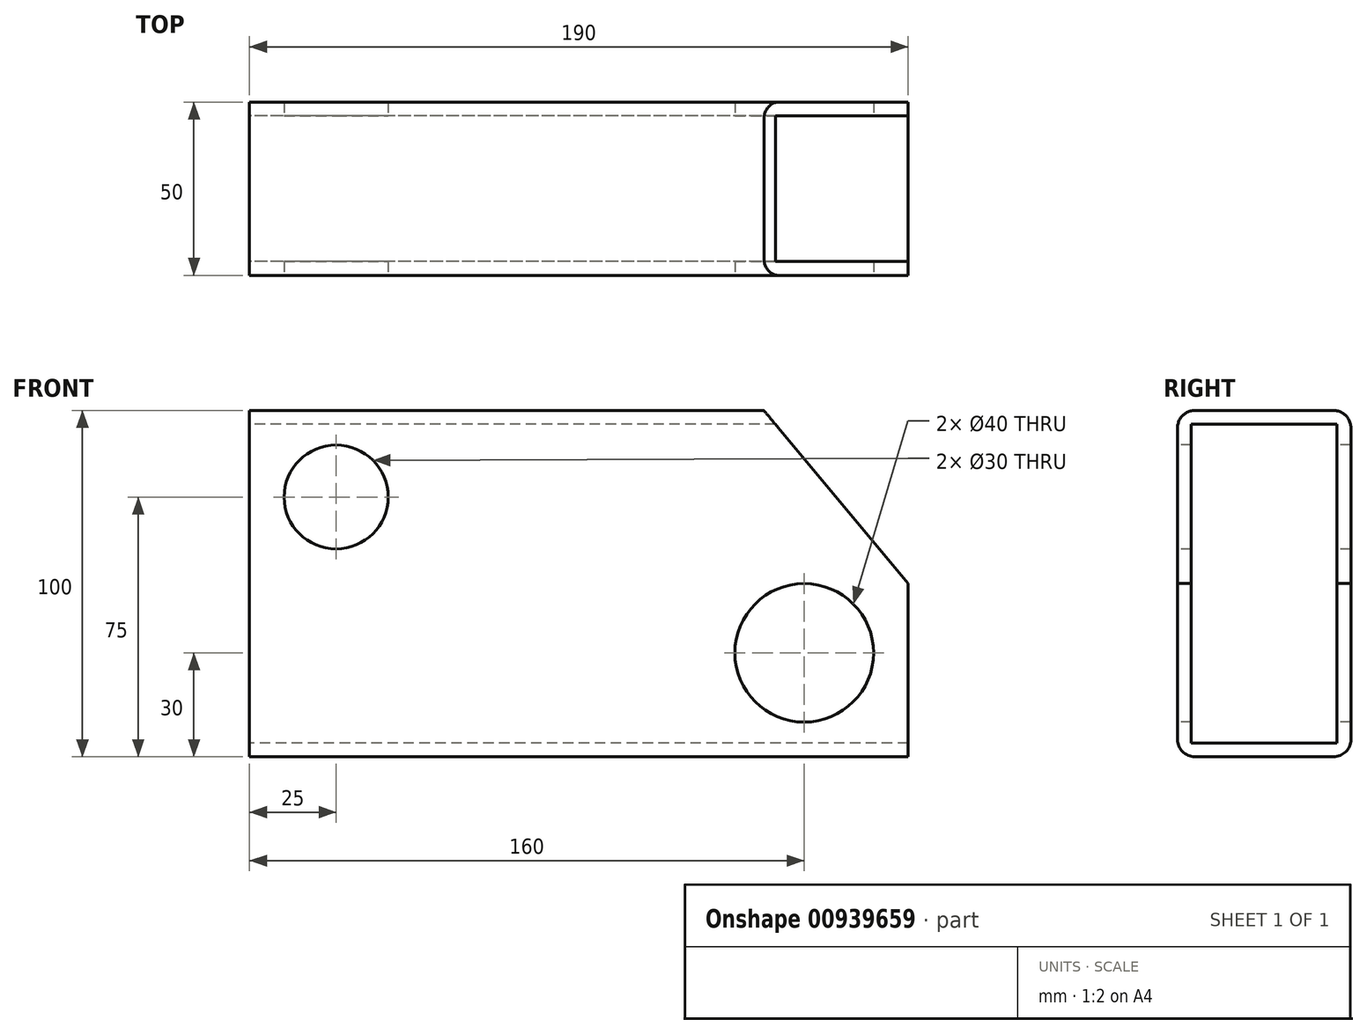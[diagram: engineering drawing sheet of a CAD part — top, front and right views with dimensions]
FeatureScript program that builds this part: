
annotation { "Feature Type Name" : "Feature", "Feature Type Description" : "" }
export const myFeature = defineFeature(function(context is Context, id is Id, definition is map)
    precondition{}
    {
        {
            var Q0;
            Q0=qCreatedBy(makeId("Front.planeOp"),FACE);
            var sketch = newSketch(context, id + "F0", { "sketchPlane" : qUnion([Q0])});
            skLineSegment(sketch, "E0.bottom", {"start": v(95, -50) * mm, "end": v(-95, -50) * mm});
            skLineSegment(sketch, "E0.top", {"start": v(53.36, 50) * mm, "end": v(-95, 50) * mm});
            skLineSegment(sketch, "E0.left", {"start": v(95, -50) * mm, "end": v(95, 0) * mm});
            skLineSegment(sketch, "E0.right", {"start": v(-95, -50) * mm, "end": v(-95, 50) * mm});
            skPoint(sketch, "E0.middle", {"position": v(0, 0) * mm});
            skLineSegment(sketch, "E1", {"start": v(53.36, 50) * mm, "end": v(95, 0) * mm});
            skPoint(sketch, "E2.orphan", {"position": v(95, 50) * mm});
            skSolve(sketch);
        }
        {
            var Q0;
            Q0=qSketchRegion(id+"F0",true);
            extrude(context, id + "F1", {"entities" : qUnion([Q0]), "oppositeDirection" : true, "depth" : 50 * mm, "offsetDistance" : 25 * mm});
        }
        {
            var Q0;
            Q0=makeQuery(id+"F1.opExtrude","SWEPT_FACE",FACE,{"disambiguationData":[OSD([sQuery(id+"F0.wireOp",EDGE,"E0.right")])]});
            var Q1;
            Q1=makeQuery(id+"F1.opExtrude","SWEPT_FACE",FACE,{"disambiguationData":[OSD([sQuery(id+"F0.wireOp",EDGE,"E0.left")])]});
            var Q2;
            Q2=makeQuery(id+"F1.opExtrude","SWEPT_FACE",FACE,{"disambiguationData":[OSD([sQuery(id+"F0.wireOp",EDGE,"E1")])]});
            shell(context, id + "F2", {"entities" : qUnion([Q0, Q1, Q2]), "thickness" : 4 * mm});
        }
        {
            var Q0;
            Q0=qCreatedBy(makeId("Front.planeOp"),FACE);
            var sketch = newSketch(context, id + "F3", { "sketchPlane" : qUnion([Q0])});
            skCircle(sketch, "E3", {"center": v(-70, 25) * mm, "radius": 15 * mm});
            skCircle(sketch, "E4", {"center": v(65, -20) * mm, "radius": 20 * mm});
            skSolve(sketch);
        }
        {
            var Q0;
            Q0=qSketchRegion(id+"F3",true);
            extrude(context, id + "F4", {"entities" : qUnion([Q0]), "operationType" : NewBodyOperationType.REMOVE, "endBound" : BoundingType.THROUGH_ALL, "oppositeDirection" : true, "depth" : 25 * mm, "offsetDistance" : 25 * mm});
        }
        {
            var Q0;
            Q0=makeQuery(id+"F1.opExtrude","CAP_EDGE",EDGE,{"disambiguationData":[OSD([sQuery(id+"F0.wireOp",EDGE,"E0.top")])],"isStart":true});
            var Q1;
            Q1=makeQuery(id+"F1.opExtrude","CAP_EDGE",EDGE,{"disambiguationData":[OSD([sQuery(id+"F0.wireOp",EDGE,"E0.top")])],"isStart":false});
            var Q2;
            Q2=makeQuery(id+"F1.opExtrude","CAP_EDGE",EDGE,{"disambiguationData":[OSD([sQuery(id+"F0.wireOp",EDGE,"E0.bottom")])],"isStart":true});
            var Q3;
            Q3=makeQuery(id+"F1.opExtrude","CAP_EDGE",EDGE,{"disambiguationData":[OSD([sQuery(id+"F0.wireOp",EDGE,"E0.bottom")])],"isStart":false});
            fillet(context, id + "F5", {"entities" : qUnion([Q0, Q1, Q2, Q3]), "radius" : 5 * mm, "tangentPropagation" : true, "allowEdgeOverflow" : false});
        }
    });
